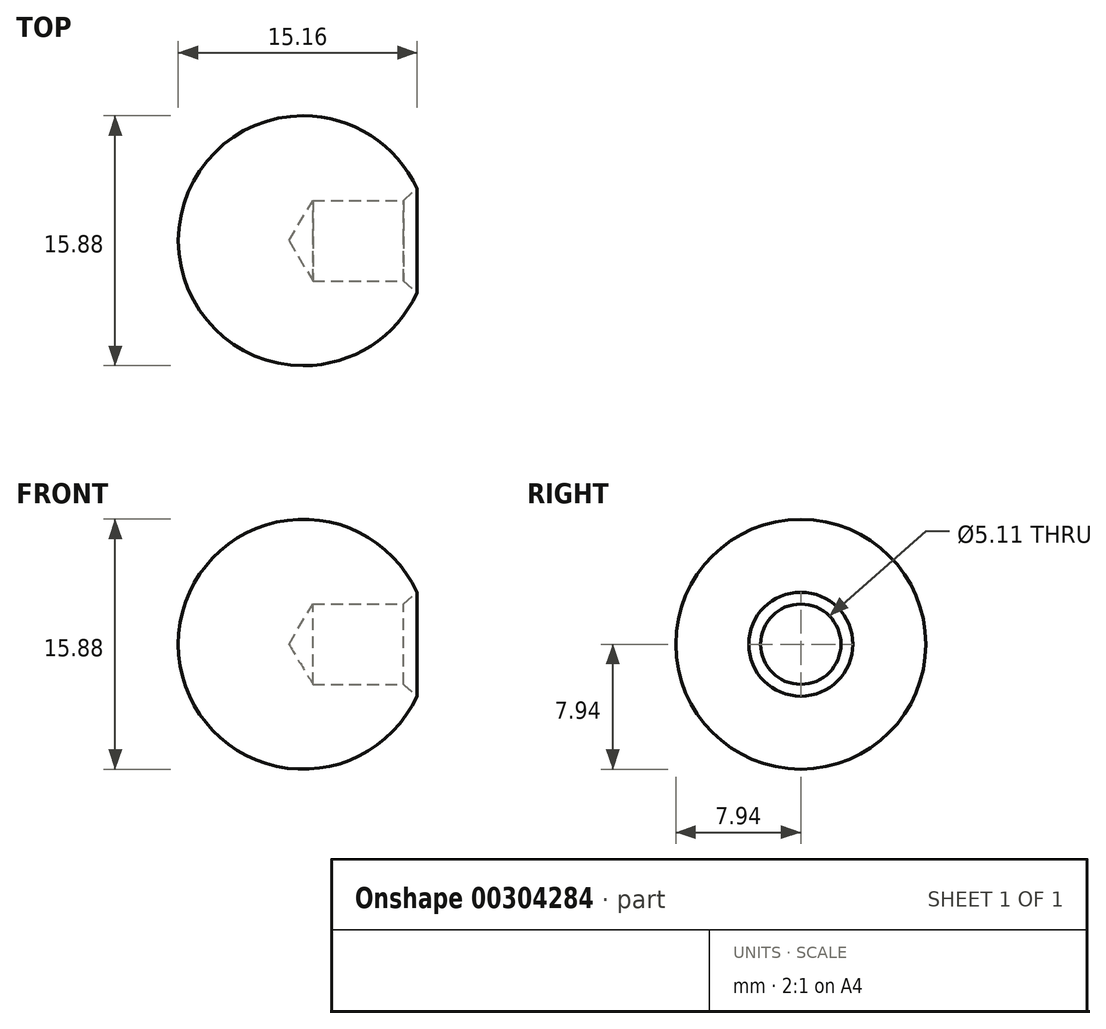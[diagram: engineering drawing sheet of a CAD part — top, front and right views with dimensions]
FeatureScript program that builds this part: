
annotation { "Feature Type Name" : "Feature", "Feature Type Description" : "" }
export const myFeature = defineFeature(function(context is Context, id is Id, definition is map)
    precondition{}
    {
        {
            var Q0;
            Q0=qCreatedBy(makeId("Top.planeOp"),FACE);
            var sketch = newSketch(context, id + "F0", { "sketchPlane" : qUnion([Q0])});
            skArc(sketch, "E0", {"start": v(0, -7.94) * mm, "mid": v(7.94, 0) * mm, "end": v(0, 7.94) * mm});
            skLineSegment(sketch, "E1", {"start": v(0, 7.94) * mm, "end": v(0, -7.94) * mm});
            skPoint(sketch, "E2", {"position": v(7.94, 0) * mm});
            skSolve(sketch);
        }
        {
            var Q0;
            Q0=makeQuery(id+"F0.imprint","IMPRINT",FACE,{"disambiguationData":[TD([[makeQuery(id+"F0.imprint","IMPRINT",EDGE,{"derivedFrom":sQuery(id+"F0.wireOp",EDGE,"E0")}),1.0]])]});
            var Q1;
            Q1=sQuery(id+"F0.wireOp",EDGE,"E1");
            revolve(context, id + "F1", {"entities" : qUnion([Q0]), "axis" : qUnion([Q1]), "revolveType" : RevolveType.FULL});
        }
        {
            var Q0;
            Q0=qCreatedBy(makeId("Right.planeOp"),FACE);
            cPlane(context, id + "F2", {"entities" : qUnion([Q0]), "cplaneType" : CPlaneType.OFFSET, "offset" : 7.94 * mm, "width" : 152.4 * mm, "height" : 152.4 * mm});
        }
        {
            var Q0;
            Q0=qCreatedBy(id+"F2.planeOp",FACE);
            var sketch = newSketch(context, id + "F3", { "sketchPlane" : qUnion([Q0])});
            skPoint(sketch, "E3", {"position": v(0, 0) * mm});
            skSolve(sketch);
        }
        {
            var Q0;
            Q0=sQuery(id+"F3.wireOp",VERTEX,"E3");
            var Q1;
            Q1=makeQuery(id+"F1.opRevolve","SWEPT_BODY",BODY,{"disambiguationData":[OSD([sQuery(id+"F0.wireOp",EDGE,"E0"),sQuery(id+"F0.wireOp",EDGE,"E1")])]});
            hole(context, id + "F4", {"style" : HoleStyle.C_SINK, "endStyle" : HoleEndStyle.BLIND, "holeDiameter" : 5.1 * mm, "cSinkDiameter" : 6.6 * mm, "cSinkAngle" : 82 * degree, "holeDepth" : 6.6 * mm, "tappedDepth" : 6.6 * mm, "tapClearance" : 3, "locations" : qUnion([Q0]), "scope" : qUnion([Q1])});
        }
    });
